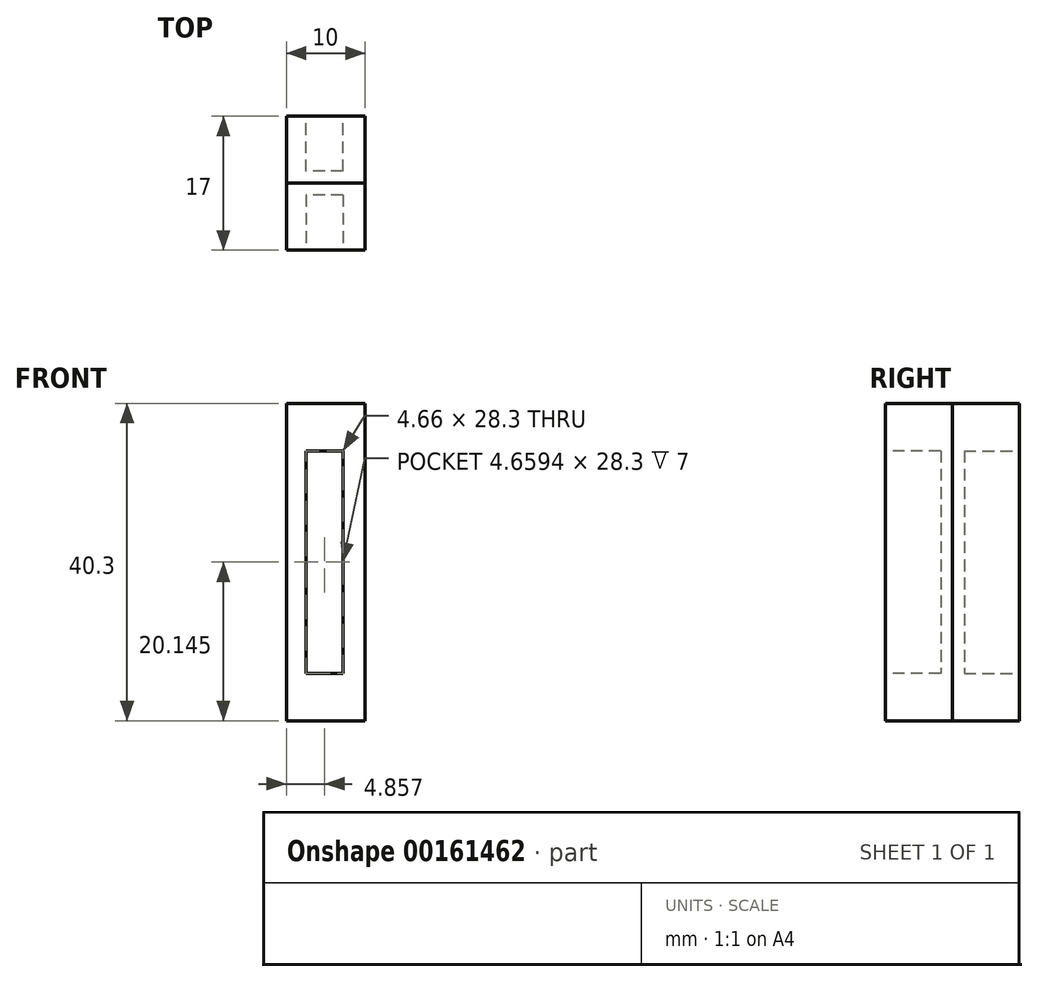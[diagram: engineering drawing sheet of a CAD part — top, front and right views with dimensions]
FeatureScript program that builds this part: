
annotation { "Feature Type Name" : "Feature", "Feature Type Description" : "" }
export const myFeature = defineFeature(function(context is Context, id is Id, definition is map)
    precondition{}
    {
        {
            var Q0;
            Q0=qCreatedBy(makeId("Front.planeOp"),FACE);
            var sketch = newSketch(context, id + "F0", { "sketchPlane" : qUnion([Q0])});
            skLineSegment(sketch, "E0.bottom", {"start": v(-30.25, -40.58) * mm, "end": v(-20.25, -40.58) * mm});
            skLineSegment(sketch, "E0.top", {"start": v(-30.25, -80.88) * mm, "end": v(-20.25, -80.88) * mm});
            skLineSegment(sketch, "E0.left", {"start": v(-30.25, -40.58) * mm, "end": v(-30.25, -80.88) * mm});
            skLineSegment(sketch, "E0.right", {"start": v(-20.25, -40.58) * mm, "end": v(-20.25, -80.88) * mm});
            skLineSegment(sketch, "E1.bottom", {"start": v(-23.06, -46.58) * mm, "end": v(-27.72, -46.58) * mm});
            skLineSegment(sketch, "E1.top", {"start": v(-23.06, -74.88) * mm, "end": v(-27.72, -74.88) * mm});
            skLineSegment(sketch, "E1.left", {"start": v(-23.06, -46.58) * mm, "end": v(-23.06, -74.88) * mm});
            skLineSegment(sketch, "E1.right", {"start": v(-27.72, -46.58) * mm, "end": v(-27.72, -74.88) * mm});
            skLineSegment(sketch, "E2", {"start": v(-23.06, -74.88) * mm, "end": v(-23.06, -80.88) * mm, "construction": true});
            skLineSegment(sketch, "E3", {"start": v(-27.72, -46.58) * mm, "end": v(-27.72, -40.58) * mm, "construction": true});
            skSolve(sketch);
        }
        {
            var Q0;
            Q0=makeQuery(id+"F0.imprint","IMPRINT",FACE,{"disambiguationData":[TD([[makeQuery(id+"F0.imprint","IMPRINT",EDGE,{"derivedFrom":sQuery(id+"F0.wireOp",EDGE,"E0.bottom")}),-1.0]])]});
            var Q1;
            Q1=makeQuery(id+"F0.imprint","IMPRINT",FACE,{"disambiguationData":[TD([[makeQuery(id+"F0.imprint","IMPRINT",EDGE,{"derivedFrom":sQuery(id+"F0.wireOp",EDGE,"0H4b4fvO-dyxi-FZrW-pJNc-f5h2Ua2qFgm1.bottom")}),-1.0]])]});
            var Q2;
            Q2=makeQuery(id+"F0.imprint","IMPRINT",FACE,{"disambiguationData":[TD([[makeQuery(id+"F0.imprint","IMPRINT",EDGE,{"derivedFrom":sQuery(id+"F0.wireOp",EDGE,"RIwqPRcQ-8Yhb-SA2c-7hZh-BoyqNhFDoh6P.bottom")}),-1.0]])]});
            var Q3;
            Q3=makeQuery(id+"F0.imprint","IMPRINT",FACE,{"disambiguationData":[TD([[makeQuery(id+"F0.imprint","IMPRINT",EDGE,{"derivedFrom":sQuery(id+"F0.wireOp",EDGE,"V1CP0RN2-3pWF-4ICx-AOtc-XG8nw0NRMOAc.bottom")}),-1.0]])]});
            var Q4;
            Q4=makeQuery(id+"F0.imprint","IMPRINT",FACE,{"disambiguationData":[TD([[makeQuery(id+"F0.imprint","IMPRINT",EDGE,{"derivedFrom":sQuery(id+"F0.wireOp",EDGE,"E1.bottom")}),1.0]])]});
            extrude(context, id + "F1", {"entities" : qUnion([Q0, Q1, Q2, Q3, Q4]), "depth" : 8.5 * mm});
        }
        {
            var Q0;
            Q0=makeQuery(id+"F0.imprint","IMPRINT",FACE,{"disambiguationData":[TD([[makeQuery(id+"F0.imprint","IMPRINT",EDGE,{"derivedFrom":sQuery(id+"F0.wireOp",EDGE,"0H4b4fvO-dyxi-FZrW-pJNc-f5h2Ua2qFgm1.bottom")}),-1.0]])]});
            var Q1;
            Q1=makeQuery(id+"F0.imprint","IMPRINT",FACE,{"disambiguationData":[TD([[makeQuery(id+"F0.imprint","IMPRINT",EDGE,{"derivedFrom":sQuery(id+"F0.wireOp",EDGE,"RIwqPRcQ-8Yhb-SA2c-7hZh-BoyqNhFDoh6P.bottom")}),-1.0]])]});
            var Q2;
            Q2=makeQuery(id+"F0.imprint","IMPRINT",FACE,{"disambiguationData":[TD([[makeQuery(id+"F0.imprint","IMPRINT",EDGE,{"derivedFrom":sQuery(id+"F0.wireOp",EDGE,"V1CP0RN2-3pWF-4ICx-AOtc-XG8nw0NRMOAc.bottom")}),-1.0]])]});
            var Q3;
            Q3=makeQuery(id+"F0.imprint","IMPRINT",FACE,{"disambiguationData":[TD([[makeQuery(id+"F0.imprint","IMPRINT",EDGE,{"derivedFrom":sQuery(id+"F0.wireOp",EDGE,"E1.bottom")}),1.0]])]});
            extrude(context, id + "F2", {"entities" : qUnion([Q0, Q1, Q2, Q3]), "operationType" : NewBodyOperationType.REMOVE, "depth" : 7 * mm});
        }
        {
            var Q0;
            Q0=makeQuery(id+"F1.opExtrude","SWEPT_BODY",BODY,{"disambiguationData":[OSD([sQuery(id+"F0.wireOp",EDGE,"E0.bottom"),sQuery(id+"F0.wireOp",EDGE,"E0.top"),sQuery(id+"F0.wireOp",EDGE,"E0.left"),sQuery(id+"F0.wireOp",EDGE,"E0.right")])]});
            var Q1;
            Q1=makeQuery(id+"F1.opExtrude","CAP_FACE",FACE,{"disambiguationData":[OSD([sQuery(id+"F0.wireOp",EDGE,"E0.bottom"),sQuery(id+"F0.wireOp",EDGE,"E0.top"),sQuery(id+"F0.wireOp",EDGE,"E0.left"),sQuery(id+"F0.wireOp",EDGE,"E0.right")])],"isStart":false});
            mirror(context, id + "F3", {"entities" : qUnion([Q0]), "mirrorPlane" : qUnion([Q1])});
        }
    });
